# Revit family: Calida standaard - 04 Details
name_source: partatom
category: Generic Models
revit_build: Autodesk Revit 2018 (Build: 20170223_1515(x64)
units: mm (PartAtom-declared; Revit-internal decimal feet)

## family parameters
Always vertical = Yes
Can host rebar = No
Cut with Voids When Loaded = No
Part Type = Normal
Room Calculation Point = No
Round Connector Dimension = Use Diameter
Shared = No
Work Plane-Based = No

## types (1)
- Calida standaard - 04 Details
    Art. No. = 300 050 004
    Bedieningspaneel = Kunststof zwart
    Brass = Brass
    Breedte = 418 mm  [stored 1.37139 ft]
    Buttons = Buttons
    Colour = Plexiglass
    Diepte = 153 mm  [stored 0.501969 ft]
    Hoogte = 710 mm
    Koper = Copper
    Kunststof 2 = Kunststof wit glad
    Kunststof paneel = Kunststof grijs
    Manufacturer = Masterwatt B.V.
    Metaal geborsteld = Metaal
    Metaal zwart = Metal black
    Model = Calida standaard - 04
    Phase = 1
    Power (default) = 4000 VA
    Transparant kunststof = Kunststof transparant
    Transparante buis = Transparant plastic
    URL = https://masterwatt.nl
    Voltage = 230 V

note: [stored X ft] marks values corroborated as IEEE doubles in the binary element streams (Revit-internal decimal feet)

## geometry (parser evidence)
native form markers: Sweep x2
no freeform markers — native parametric forms only
